# Revit family: QF_RATIONAL_CombiSteamer_iCP_6-11E
name_source: partatom
category: Specialty Equipment
revit_build: Autodesk Revit 2018 (Build: 20170223_1515(x64)
units: mm (PartAtom-declared; Revit-internal decimal feet)

## family parameters
Always vertical = Yes
Cut with Voids When Loaded = No
OmniClass Number = 23.40.40.14.17.11
OmniClass Title = Cookers, Ovens, Stoves
Part Type = Normal
Room Calculation Point = No
Round Connector Dimension = Use Diameter
Shared = No
Work Plane-Based = No

## types (17) — shared parameters
Assembly Code = E1090320
Cold Water Flow = 0.2 L/s
Cold Water Maximum Pressure = 6.0 bar
Cold Water Minimum Pressure = 1.0 bar
Cold Water Size = 1"
Conn Conduit = Yes
Cycle = 50 Hz
Cycle Alternative = 60 Hz
Depth Actual = 775 mm
Description = Electrical Combi-steamer (6 x 1/1 GN / 12 x 1/2 GN)
Direct Waste Size = 2"
Height Actual = 756 mm
Hood Exhaust Hood = Hood : Exhaust Hood
Hood UltraVent = Hood : UltraVent
Hood UltraVent Plus = Hood : UltraVent Plus
Kit with Rollers = Accessories : Adjustable Rollers
Latent Heat Output = 1 kW
Length Actual = 851 mm
Manufacturer = RATIONAL AG
Model = iCombi Pro 6-1/1  E
Sensitive Heat Output = 1 kW
Sound Level = 55dBA
Specification by Manufacturer = Hot-air steamer (combi-steamer mode) for most of the cooking methods used in commercial kitchens for the optional use of steam and hot-air, individually, in succession or in combination.
Stand Levelling Kit = Accessories : Levelling Kit
Stand None = Accessories : None
Stand UG I 150 = Accessories : UG I 150
Stand UG I 200 = Accessories : UG I 200
Stand UG I 699 = Accessories : UG I 699
Stand UG II 699 = Accessories : UG II 699
Stand UG III 699 = Accessories : UG III 699
Stand UG III 945 = Accessories : UG III 945
Stand UG IV 699 = Accessories : UG IV 699
URL = www.rational-online.com
Version = 05-2020
Warranty Duration = 2 years
Waste Water Discharge Temperature = 65 °C
Weight = 99.00 kg

## per-type parameters (varying)
| type | FL Amps | Max Overcurrent Protection | Phase | Volts | Watts |
| 6-1/1E 3 AC 415V | 15 A | 16 A | 3 | 415 V | 10800 W |
| 6-1/1E 3 AC 208V | 30 A | 40 A | 3 | 208 V | 10800 W |
| 6-1/1E 3 AC 220V (Korea) | 26 A | 32 A | 3 | 220 V | 9900 W |
| 6-1/1E 3 AC 220V | 26 A | 32 A | 3 | 220 V | 9900 W |
| 6-1/1E 3NAC 415V | 15 A | 16 A | 3 | 415 V | 10800 W |
| 6-1/1E 3NAC 400V | 16 A | 16 A | 3 | 400 V | 10800 W |
| 6-1/1E 3AC 480V | 13 A | 16 A | 3 | 480 V | 10800 W |
| 6-1/1E 3AC 440V | 14 A | 16 A | 3 | 440 V | 10800 W |
| 6-1/1E 3AC 400V | 16 A | 16 A | 3 | 400 V | 10800 W |
| 6-1/1E 3AC 240V | 28 A | 70 A | 3 | 240 V | 11700 W |
| 6-1/1E 3AC 230V | 27 A | 32 A | 3 | 230 V | 10800 W |
| 6-1/1E 3AC 200V | 29 A | 32 A | 3 | 200 V | 10000 W |
| 6-1/1E 2AC 240V | 49 A | 70 A | 2 | 240 V | 11700 W |
| 6-1/1E 2AC 230V | 47 A | 50 A | 2 | 230 V | 10800 W |
| 6-1/1E 2AC 208V | 52 A | 70 A | 2 | 208 V | 10800 W |
| 6-1/1E 1NAC 240V | 48 A | 50 A | 1 | 240 V | 11700 W |
| 6-1/1E 1NAC 230V | 47 A | 50 A | 1 | 230 V | 10800 W |

## geometry (parser evidence)
native form markers: Sweep x21
no freeform markers — native parametric forms only
